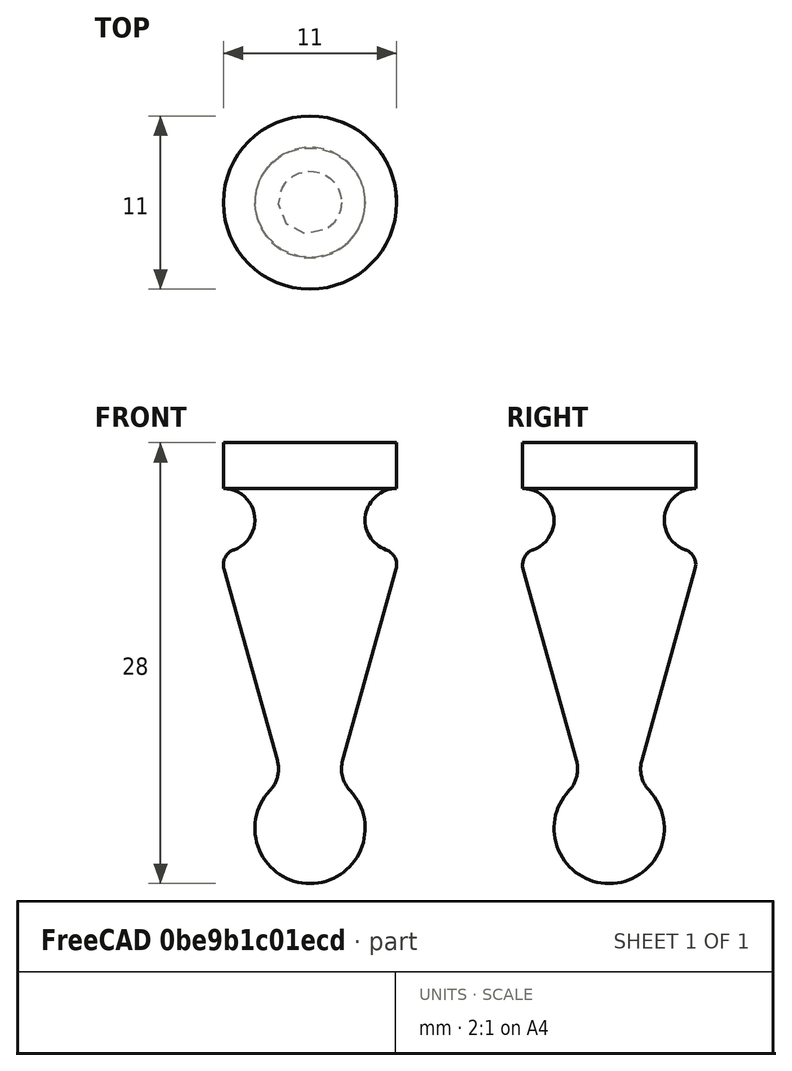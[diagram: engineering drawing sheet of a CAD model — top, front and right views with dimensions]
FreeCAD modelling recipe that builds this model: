
FCSTD DOCUMENT  (FreeCAD 2022.709R28846 (Git))
Label: fischband_zierelement
License: All rights reserved
LicenseURL: http://en.wikipedia.org/wiki/All_rights_reserved
objects: Sketcher::SketchObject×1, PartDesign::Revolution×1, PartDesign::Body×1
note: 5 computed .brp shape members not serialized (recipe doc carries the construction recipe); baked Part::Feature solids carry a one-line shape summary decoded from their .brp

FEATURE [Sketcher::SketchObject] Sketch
  ArcFitTolerance = 1e-06
  AttachmentSupport = -> [XZ_Plane]
  FullyConstrained = true
  MapMode = 5
  Placement = pos=(0,0,0) rot=(1,0,0;1.5708rad)
  Support = -> [XZ_Plane]
  TreeRank = 13
  sketch-geometry (9):
    g0: LineSegment StartX=0 StartY=0 StartZ=0 EndX=0 EndY=-28 EndZ=0
    g1: LineSegment StartX=5.46337 StartY=-8.011 StartZ=0 EndX=2.07327 EndY=-20.1887 EndZ=0
    g2: ArcOfCircle CenterX=0 CenterY=-24.5 CenterZ=0 NormalX=0 NormalY=0 NormalZ=1 AngleXU=0 Radius=3.5 StartAngle=4.71239 EndAngle=7.03964
    g3: ArcOfCircle CenterX=5.5 CenterY=-4.91438 CenterZ=0 NormalX=0 NormalY=0 NormalZ=1 AngleXU=0 Radius=2 StartAngle=1.5708 EndAngle=4.37255
    g4: ArcOfCircle CenterX=4.5 CenterY=-7.74281 CenterZ=0 NormalX=0 NormalY=0 NormalZ=1 AngleXU=0 Radius=1 StartAngle=6.01167 EndAngle=7.51414
    g5: ArcOfCircle CenterX=4 CenterY=-20.7251 CenterZ=0 NormalX=0 NormalY=0 NormalZ=1 AngleXU=0 Radius=2 StartAngle=2.87008 EndAngle=3.89805
    g6: LineSegment StartX=5.5 StartY=-2.91438 StartZ=0 EndX=5.5 EndY=0 EndZ=0
    g7: LineSegment StartX=5.5 StartY=0 StartZ=0 EndX=0 EndY=0 EndZ=0
    g8: LineSegment [constr] StartX=5.5 StartY=0 StartZ=0 EndX=5.5 EndY=-10 EndZ=0
  constraints (26):
    c: Vertical(g0)
    c: Coincident(g2,g0)
    c: Radius(g2) = 3.5
    c: DistanceX(g0,g3) = 5.5
    c: Tangent(g1,g4) = 1.5708
    c: Tangent(g2,g5) = 1.5708
    c: Tangent(g1,g5) = -1.5708
    c: Radius(g5) = 2
    c: Radius(g4) = 1
    c: Radius(g3) = 2
    c: DistanceX(g0,g5) = 4
    c: Tangent(g3,g4) = 1.5708
    c: PointOnObject(g2,g0)
    c: Coincident(g6,g7)
    c: Horizontal(g7)
    c: Vertical(g6)
    c: DistanceY(g0,g7) = 28
    c: DistanceY(g3,g7) = 6.8
    c: Coincident(g0,g7)
    c: Coincident(g3,g6)
    c: Coincident(g0,g-1)
    c: Coincident(g8,g6)
    c: Vertical(g8)
    c: Tangent(g8,g4)
    c: PointOnObject(g3,g8)
    c: DistanceY(g8,g8) = 10
FEATURE [PartDesign::Revolution] Revolution
  Angle = 360
  Axis = (0,-2e-16,1)
  Base = (0,0,0)
  ClaimChildren = false
  Fit = 0
  FitJoin = 0
  InnerFit = 0
  InnerFitJoin = 0
  NewSolid = false
  Placement = pos=(0,0,0) rot=(1,0,0;1.5708rad)
  Profile = -> Sketch
  ReferenceAxis = -> Sketch [V_Axis]
  Refine = true
  Reversed = true
  Suppress = false
  TreeRank = 14
  _ProfileBasedVersion = 1
FEATURE [PartDesign::Body] Body
  AutoGroupSolids = false
  ClaimAllChildren = false
  ExportMode = 0
  Group = -> [Sketch,Revolution]
  Origin = -> Origin
  Tip = -> Revolution
  TreeRank = 12
  _ExportChildren = -> [Revolution]
  _GroupVersion = 1
